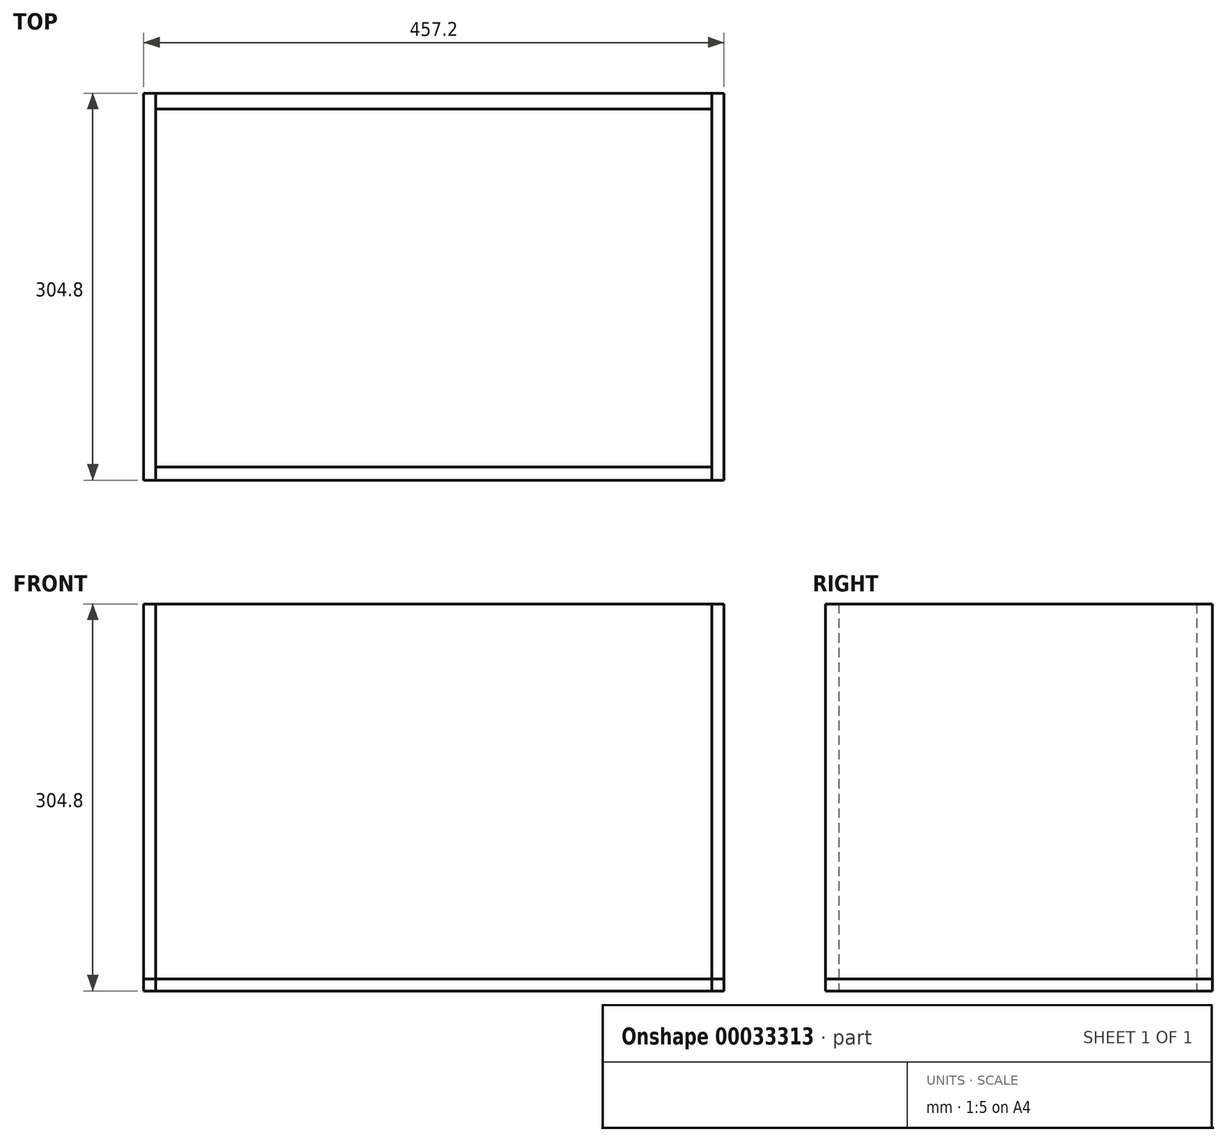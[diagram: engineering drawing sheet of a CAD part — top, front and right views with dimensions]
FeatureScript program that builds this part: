
annotation { "Feature Type Name" : "Feature", "Feature Type Description" : "" }
export const myFeature = defineFeature(function(context is Context, id is Id, definition is map)
    precondition{}
    {
        {
            var Q0;
            Q0=qCreatedBy(makeId("Top.planeOp"),FACE);
            var sketch = newSketch(context, id + "F0", { "sketchPlane" : qUnion([Q0])});
            skLineSegment(sketch, "E0.rect.bottom", {"start": v(219.08, 152.4) * mm, "end": v(-219.08, 152.4) * mm});
            skLineSegment(sketch, "E0.rect.top", {"start": v(219.08, 139.92) * mm, "end": v(-219.08, 139.92) * mm});
            skLineSegment(sketch, "E0.rect.left", {"start": v(219.08, 152.4) * mm, "end": v(219.08, 139.92) * mm});
            skLineSegment(sketch, "E0.rect.right", {"start": v(-219.08, 152.4) * mm, "end": v(-219.08, 139.92) * mm});
            skPoint(sketch, "E0.rect.middle", {"position": v(0, 146.16) * mm});
            skLineSegment(sketch, "E1.rect.bottom", {"start": v(219.08, -152.4) * mm, "end": v(-219.08, -152.4) * mm});
            skLineSegment(sketch, "E1.rect.top", {"start": v(219.08, -142) * mm, "end": v(-219.08, -142) * mm});
            skLineSegment(sketch, "E1.rect.left", {"start": v(219.08, -152.4) * mm, "end": v(219.08, -142) * mm});
            skLineSegment(sketch, "E1.rect.right", {"start": v(-219.07, -152.4) * mm, "end": v(-219.07, -142) * mm});
            skPoint(sketch, "E1.rect.middle", {"position": v(0, -147.2) * mm});
            skSolve(sketch);
        }
        {
            var Q0;
            Q0=qCreatedBy(makeId("Top.planeOp"),FACE);
            var sketch = newSketch(context, id + "F1", { "sketchPlane" : qUnion([Q0])});
            skPoint(sketch, "E2.0", {"position": v(-219.08, 152.4) * mm});
            skPoint(sketch, "E3.0", {"position": v(-219.07, -152.4) * mm});
            skPoint(sketch, "E4.0", {"position": v(219.08, -152.4) * mm});
            skPoint(sketch, "E5.0", {"position": v(219.08, 152.4) * mm});
            skLineSegment(sketch, "E6.bottom", {"start": v(-219.08, 152.4) * mm, "end": v(-228.6, 152.4) * mm});
            skLineSegment(sketch, "E6.top", {"start": v(-219.08, -152.4) * mm, "end": v(-228.6, -152.4) * mm});
            skLineSegment(sketch, "E6.left", {"start": v(-219.08, 152.4) * mm, "end": v(-219.08, -152.4) * mm});
            skLineSegment(sketch, "E6.right", {"start": v(-228.6, 152.4) * mm, "end": v(-228.6, -152.4) * mm});
            skLineSegment(sketch, "E7.bottom", {"start": v(219.08, 152.4) * mm, "end": v(228.6, 152.4) * mm});
            skLineSegment(sketch, "E7.top", {"start": v(219.08, -152.4) * mm, "end": v(228.6, -152.4) * mm});
            skLineSegment(sketch, "E7.left", {"start": v(219.08, 152.4) * mm, "end": v(219.08, -152.4) * mm});
            skLineSegment(sketch, "E7.right", {"start": v(228.6, 152.4) * mm, "end": v(228.6, -152.4) * mm});
            skSolve(sketch);
        }
        {
            var Q0;
            Q0 = qSketchRegion(id + "F0", true);
            extrude(context, id + "F2", {"entities" : qUnion([Q0]), "depth" : 304.8 * mm});
        }
        {
            var Q0;
            Q0 = qSketchRegion(id + "F1", true);
            extrude(context, id + "F3", {"entities" : qUnion([Q0]), "depth" : 304.8 * mm});
        }
        {
            var Q0;
            Q0=qCreatedBy(makeId("Top.planeOp"),FACE);
            var sketch = newSketch(context, id + "F4", { "sketchPlane" : qUnion([Q0])});
            skPoint(sketch, "E8.0", {"position": v(228.6, 152.4) * mm});
            skPoint(sketch, "E9.0", {"position": v(-228.6, -152.4) * mm});
            skLineSegment(sketch, "E10.bottom", {"start": v(228.6, 152.4) * mm, "end": v(-228.6, 152.4) * mm});
            skLineSegment(sketch, "E10.top", {"start": v(228.6, -152.4) * mm, "end": v(-228.6, -152.4) * mm});
            skLineSegment(sketch, "E10.left", {"start": v(228.6, 152.4) * mm, "end": v(228.6, -152.4) * mm});
            skLineSegment(sketch, "E10.right", {"start": v(-228.6, 152.4) * mm, "end": v(-228.6, -152.4) * mm});
            skSolve(sketch);
        }
        {
            var Q0;
            Q0 = qSketchRegion(id + "F4", true);
            extrude(context, id + "F5", {"entities" : qUnion([Q0]), "depth" : 9.52 * mm});
        }
    });
